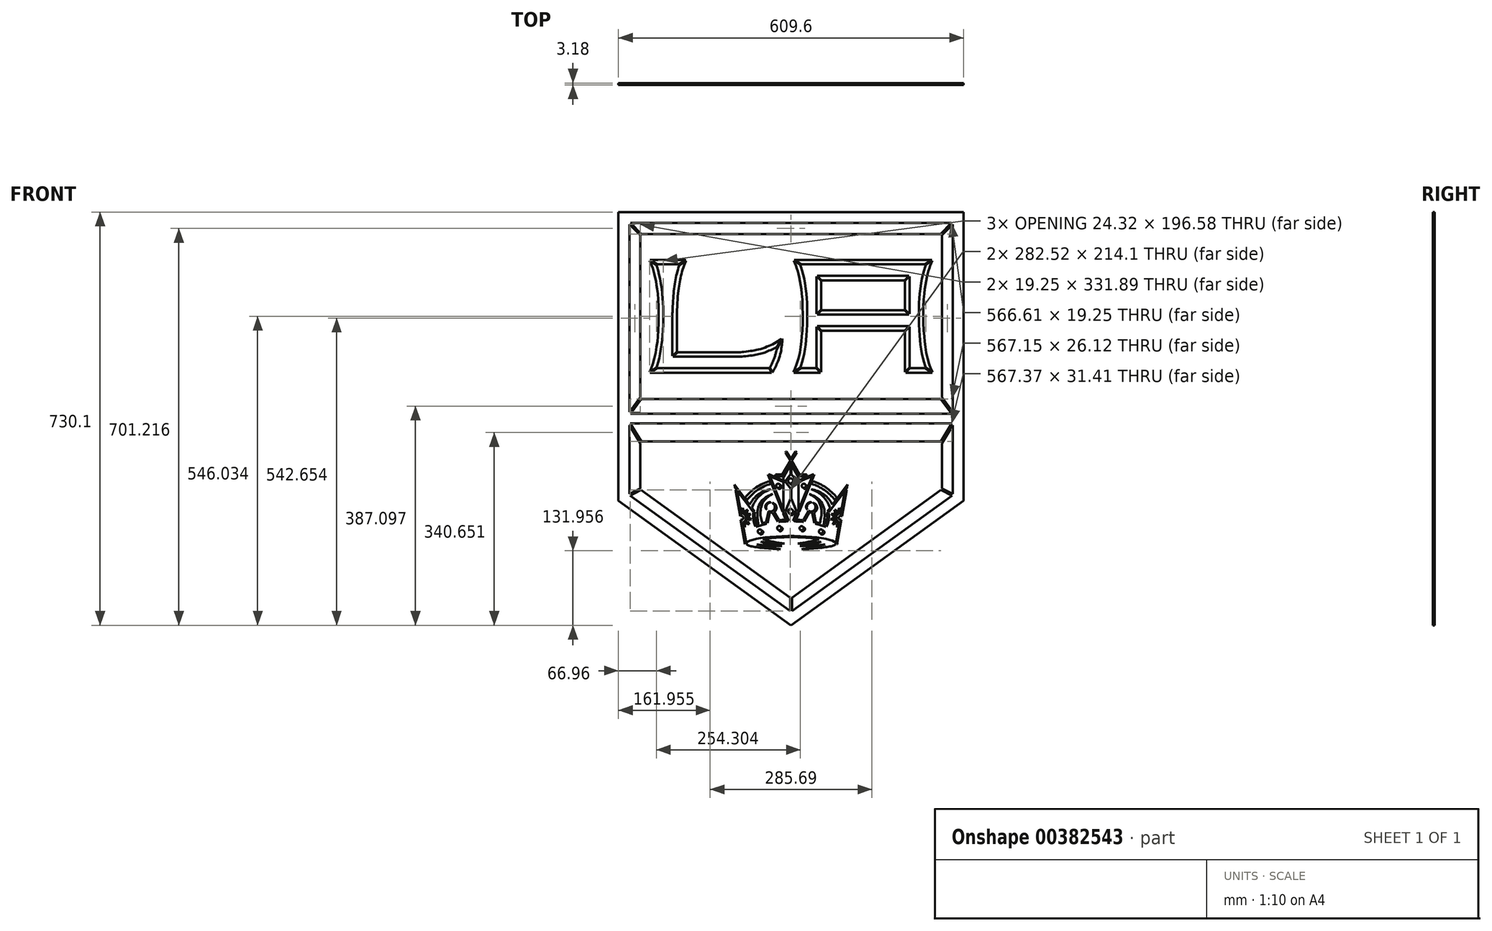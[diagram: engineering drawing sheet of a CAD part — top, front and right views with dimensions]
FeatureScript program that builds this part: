
annotation { "Feature Type Name" : "Feature", "Feature Type Description" : "" }
export const myFeature = defineFeature(function(context is Context, id is Id, definition is map)
    precondition{}
    {
        {
            var Q0;
            Q0=qCreatedBy(makeId("Front.planeOp"),FACE);
            var sketch = newSketch(context, id + "F0", { "sketchPlane" : qUnion([Q0])});
            skLineSegment(sketch, "E0", {"start": v(0, 0) * mm, "end": v(-304.8, 220.37) * mm});
            skLineSegment(sketch, "E1", {"start": v(-304.8, 220.37) * mm, "end": v(-304.8, 730.1) * mm});
            skLineSegment(sketch, "E2", {"start": v(-304.8, 730.1) * mm, "end": v(304.8, 730.1) * mm});
            skLineSegment(sketch, "E3", {"start": v(-1.59, 24.9) * mm, "end": v(-284.1, 229.17) * mm});
            skLineSegment(sketch, "E4", {"start": v(-1.59, 48.66) * mm, "end": v(-264.85, 239) * mm});
            skLineSegment(sketch, "E5", {"start": v(-285.55, 232) * mm, "end": v(-285.55, 353.32) * mm});
            skLineSegment(sketch, "E6", {"start": v(-266.3, 241.83) * mm, "end": v(-266.3, 321.91) * mm});
            skLineSegment(sketch, "E7", {"start": v(264.43, 324.95) * mm, "end": v(-264.43, 324.95) * mm});
            skLineSegment(sketch, "E8", {"start": v(283.69, 356.35) * mm, "end": v(-283.69, 356.35) * mm});
            skLineSegment(sketch, "E9", {"start": v(283.58, 374.04) * mm, "end": v(-283.58, 374.04) * mm});
            skLineSegment(sketch, "E10", {"start": v(264.32, 400.16) * mm, "end": v(-264.32, 400.16) * mm});
            skLineSegment(sketch, "E11", {"start": v(-283.3, 710.84) * mm, "end": v(283.3, 710.84) * mm});
            skLineSegment(sketch, "E12", {"start": v(-264.05, 691.59) * mm, "end": v(264.05, 691.59) * mm});
            skLineSegment(sketch, "E13", {"start": v(304.8, 220.37) * mm, "end": v(304.8, 730.1) * mm});
            skLineSegment(sketch, "E14", {"start": v(1.59, 24.9) * mm, "end": v(284.1, 229.17) * mm});
            skLineSegment(sketch, "E15", {"start": v(1.59, 48.66) * mm, "end": v(264.85, 239) * mm});
            skLineSegment(sketch, "E16", {"start": v(285.55, 232) * mm, "end": v(285.55, 353.32) * mm});
            skLineSegment(sketch, "E17", {"start": v(266.3, 241.83) * mm, "end": v(266.3, 321.91) * mm});
            skLineSegment(sketch, "E18", {"start": v(285.55, 376.71) * mm, "end": v(285.55, 708.6) * mm});
            skLineSegment(sketch, "E19", {"start": v(266.3, 402.83) * mm, "end": v(266.3, 689.34) * mm});
            skLineSegment(sketch, "E20", {"start": v(-285.55, 376.71) * mm, "end": v(-285.55, 708.6) * mm});
            skLineSegment(sketch, "E21", {"start": v(-266.3, 402.83) * mm, "end": v(-266.3, 689.34) * mm});
            skFitSpline(sketch, "E22", {"points": [v(-250, 447.75) * mm, v(-248.85, 449.98) * mm, v(-246.49, 454.7) * mm, v(-243.62, 462.95) * mm, v(-240.96, 472.2) * mm, v(-238.59, 483.4) * mm, v(-237.2, 493.08) * mm, v(-235.86, 501.9) * mm, v(-235.2, 509.36) * mm, v(-234.44, 519.64) * mm, v(-233.5, 537.38) * mm, v(-233.7, 556.74) * mm, v(-234.2, 574.6) * mm, v(-235.16, 584.45) * mm, v(-236.1, 591.32) * mm, v(-236.62, 596.69) * mm, v(-237.49, 601.42) * mm, v(-238.28, 606.78) * mm, v(-239.24, 611.8) * mm, v(-240.2, 616.28) * mm, v(-241.07, 619.38) * mm, v(-241.6, 622.23) * mm, v(-242.48, 624.82) * mm, v(-242.97, 627.3) * mm, v(-243.89, 629.6) * mm, v(-244.64, 631.93) * mm, v(-245.3, 634.07) * mm, v(-246, 635.97) * mm, v(-246.68, 637.82) * mm, v(-247.93, 640.58) * mm, v(-248.84, 642.79) * mm, v(-249.56, 644.32) * mm]});
            skFitSpline(sketch, "E23", {"points": [v(-185.13, 644.3) * mm, v(-185.73, 643.2) * mm, v(-186.9, 640.95) * mm, v(-188.33, 637.53) * mm, v(-189.8, 633.78) * mm, v(-190.93, 630.19) * mm, v(-192.11, 626.14) * mm, v(-193.33, 621.76) * mm, v(-194.58, 617.13) * mm, v(-195.4, 612.86) * mm, v(-196.19, 609.14) * mm, v(-196.86, 605.16) * mm, v(-197.56, 600.86) * mm, v(-198.28, 595.98) * mm, v(-198.96, 590.3) * mm, v(-199.73, 582.95) * mm, v(-200.48, 573.3) * mm, v(-201.11, 561.51) * mm, v(-201.45, 552.88) * mm, v(-201.47, 548.46) * mm]});
            skLineSegment(sketch, "E24", {"start": v(-201.47, 548.46) * mm, "end": v(-201.47, 483.77) * mm});
            skLineSegment(sketch, "E25", {"start": v(-200.4, 482.7) * mm, "end": v(-88.87, 482.7) * mm});
            skFitSpline(sketch, "E26", {"points": [v(-88.87, 482.7) * mm, v(-85.24, 482.97) * mm, v(-79.56, 483.4) * mm, v(-72.53, 484.53) * mm, v(-67.84, 485.1) * mm, v(-64.14, 485.99) * mm, v(-60.81, 486.73) * mm, v(-54.68, 487.7) * mm, v(-47.88, 489.83) * mm, v(-41.15, 492.84) * mm, v(-35.57, 494.86) * mm, v(-30.18, 497.95) * mm, v(-24.59, 500.93) * mm, v(-20.7, 504.2) * mm, v(-18.31, 505.7) * mm, v(-17.31, 506.57) * mm]});
            skFitSpline(sketch, "E27", {"points": [v(-15.59, 506.6) * mm, v(-15.55, 504.5) * mm, v(-15.55, 500.41) * mm, v(-16.7, 492.3) * mm, v(-18.23, 482) * mm, v(-21.17, 471.92) * mm, v(-24.25, 463.71) * mm, v(-27.07, 457.54) * mm, v(-29.96, 451.9) * mm, v(-32, 448.5) * mm, v(-32.88, 447.14) * mm]});
            skLineSegment(sketch, "E28", {"start": v(-34.23, 446.42) * mm, "end": v(-249.23, 446.42) * mm});
            skLineSegment(sketch, "E29", {"start": v(-248.81, 645.66) * mm, "end": v(-185.84, 645.66) * mm});
            skFitSpline(sketch, "E30", {"points": [v(4.3, 447.75) * mm, v(5.45, 449.98) * mm, v(7.82, 454.7) * mm, v(10.68, 462.95) * mm, v(13.35, 472.2) * mm, v(15.72, 483.4) * mm, v(17.1, 493.08) * mm, v(18.44, 501.9) * mm, v(19.1, 509.36) * mm, v(19.87, 519.64) * mm, v(20.8, 537.38) * mm, v(20.6, 556.74) * mm, v(20.1, 574.6) * mm, v(19.15, 584.45) * mm, v(18.21, 591.32) * mm, v(17.69, 596.69) * mm, v(16.82, 601.42) * mm, v(16.02, 606.78) * mm, v(15.06, 611.8) * mm, v(14.1, 616.28) * mm, v(13.23, 619.38) * mm, v(12.7, 622.23) * mm, v(11.83, 624.82) * mm, v(11.34, 627.3) * mm, v(10.42, 629.6) * mm, v(9.67, 631.93) * mm, v(9, 634.07) * mm, v(8.3, 635.97) * mm, v(7.63, 637.82) * mm, v(6.38, 640.58) * mm, v(5.47, 642.79) * mm, v(4.74, 644.32) * mm]});
            skLineSegment(sketch, "E31", {"start": v(5.5, 645.66) * mm, "end": v(248.81, 645.66) * mm});
            skLineSegment(sketch, "E32", {"start": v(249.23, 446.42) * mm, "end": v(202.36, 446.42) * mm});
            skFitSpline(sketch, "E33", {"points": [v(250, 447.75) * mm, v(248.85, 449.98) * mm, v(246.49, 454.7) * mm, v(243.62, 462.95) * mm, v(240.96, 472.2) * mm, v(238.59, 483.4) * mm, v(237.2, 493.08) * mm, v(235.86, 501.9) * mm, v(235.2, 509.36) * mm, v(234.44, 519.64) * mm, v(233.5, 537.38) * mm, v(233.7, 556.74) * mm, v(234.2, 574.6) * mm, v(235.16, 584.45) * mm, v(236.1, 591.32) * mm, v(236.62, 596.69) * mm, v(237.49, 601.42) * mm, v(238.28, 606.78) * mm, v(239.24, 611.8) * mm, v(240.2, 616.28) * mm, v(241.07, 619.38) * mm, v(241.6, 622.23) * mm, v(242.48, 624.82) * mm, v(242.97, 627.3) * mm, v(243.89, 629.6) * mm, v(244.64, 631.93) * mm, v(245.3, 634.07) * mm, v(246, 635.97) * mm, v(246.68, 637.82) * mm, v(247.93, 640.58) * mm, v(248.84, 642.79) * mm, v(249.56, 644.32) * mm]});
            skLineSegment(sketch, "E34", {"start": v(54.1, 609.59) * mm, "end": v(200.2, 609.59) * mm});
            skLineSegment(sketch, "E35", {"start": v(54.1, 556.91) * mm, "end": v(200.2, 556.91) * mm});
            skLineSegment(sketch, "E36", {"start": v(54.1, 520.58) * mm, "end": v(200.2, 520.58) * mm});
            skLineSegment(sketch, "E37", {"start": v(53.02, 447.5) * mm, "end": v(53.02, 519.5) * mm});
            skLineSegment(sketch, "E38", {"start": v(201.28, 447.5) * mm, "end": v(201.28, 519.5) * mm});
            skLineSegment(sketch, "E39", {"start": v(51.94, 446.42) * mm, "end": v(5.07, 446.42) * mm});
            skLineSegment(sketch, "E40", {"start": v(53.02, 558) * mm, "end": v(53.02, 608.5) * mm});
            skLineSegment(sketch, "E41", {"start": v(201.28, 558) * mm, "end": v(201.28, 608.5) * mm});
            skLineSegment(sketch, "E42", {"start": v(-8.97, 307.2) * mm, "end": v(-9.82, 305.39) * mm});
            skLineSegment(sketch, "E43", {"start": v(-8.25, 307.2) * mm, "end": v(-8.97, 307.2) * mm});
            skLineSegment(sketch, "E44", {"start": v(-1.08, 291.22) * mm, "end": v(-15.16, 266.73) * mm});
            skLineSegment(sketch, "E45", {"start": v(-99.7, 248.48) * mm, "end": v(-98.64, 242.38) * mm});
            skArc(sketch, "E46", {"start": v(-36.02, 249.87) * mm, "mid": v(-59.07, 238.98) * mm, "end": v(-77.5, 221.37) * mm});
            skLineSegment(sketch, "E47", {"start": v(-14.4, 263.48) * mm, "end": v(-26.33, 263.48) * mm});
            skLineSegment(sketch, "E48", {"start": v(-27.56, 266.73) * mm, "end": v(-15.16, 266.73) * mm});
            skLineSegment(sketch, "E49", {"start": v(-1.08, 291.22) * mm, "end": v(-9.82, 305.39) * mm});
            skArc(sketch, "E50", {"start": v(-27.56, 266.73) * mm, "mid": v(-27.25, 265) * mm, "end": v(-26.33, 263.48) * mm});
            skCircle(sketch, "E51", {"center": v(-20.88, 171.82) * mm, "radius": 3.66 * mm});
            skArc(sketch, "E52", {"start": v(-20.53, 166.47) * mm, "mid": v(-15.9, 167.81) * mm, "end": v(-15.58, 172.62) * mm});
            skArc(sketch, "E53", {"start": v(-20.45, 166.95) * mm, "mid": v(-16.9, 168.62) * mm, "end": v(-16.03, 172.44) * mm});
            skCircle(sketch, "E54", {"center": v(-55.14, 165.94) * mm, "radius": 3.66 * mm});
            skArc(sketch, "E55", {"start": v(-54.79, 160.6) * mm, "mid": v(-50.17, 161.93) * mm, "end": v(-49.84, 166.74) * mm});
            skArc(sketch, "E56", {"start": v(-54.7, 161.07) * mm, "mid": v(-51.16, 162.74) * mm, "end": v(-50.29, 166.56) * mm});
            skCircle(sketch, "E57", {"center": v(18.65, 171.41) * mm, "radius": 3.66 * mm});
            skArc(sketch, "E58", {"start": v(19, 166.06) * mm, "mid": v(23.62, 167.4) * mm, "end": v(23.95, 172.21) * mm});
            skArc(sketch, "E59", {"start": v(19.08, 166.54) * mm, "mid": v(22.62, 168.21) * mm, "end": v(23.5, 172.03) * mm});
            skCircle(sketch, "E60", {"center": v(52.9, 165.74) * mm, "radius": 3.66 * mm});
            skArc(sketch, "E61", {"start": v(53.25, 160.39) * mm, "mid": v(57.88, 161.73) * mm, "end": v(58.2, 166.54) * mm});
            skArc(sketch, "E62", {"start": v(53.34, 160.87) * mm, "mid": v(56.88, 162.54) * mm, "end": v(57.76, 166.35) * mm});
            skLineSegment(sketch, "E63", {"start": v(-10.12, 200.44) * mm, "end": v(-3.9, 184.71) * mm});
            skLineSegment(sketch, "E64", {"start": v(-13.2, 262.24) * mm, "end": v(-13.2, 254.89) * mm});
            skLineSegment(sketch, "E65", {"start": v(-10.12, 200.44) * mm, "end": v(-0.8, 224.23) * mm});
            skLineSegment(sketch, "E66", {"start": v(-0.83, 242.03) * mm, "end": v(-9.69, 253.36) * mm});
            skLineSegment(sketch, "E67", {"start": v(-9.72, 254.89) * mm, "end": v(-0.77, 267.03) * mm});
            skLineSegment(sketch, "E68", {"start": v(-67.1, 200.23) * mm, "end": v(-98.64, 242.38) * mm});
            skLineSegment(sketch, "E69", {"start": v(-41.4, 180.52) * mm, "end": v(-37.35, 199.4) * mm});
            skLineSegment(sketch, "E70", {"start": v(-23.32, 183.5) * mm, "end": v(-32.34, 199.14) * mm});
            skArc(sketch, "E71", {"start": v(-35.66, 240.3) * mm, "mid": v(-57.84, 231.32) * mm, "end": v(-73.04, 212.85) * mm});
            skArc(sketch, "E72", {"start": v(-35.66, 240.3) * mm, "mid": v(-56.4, 227.88) * mm, "end": v(-68.76, 207.13) * mm});
            skFitSpline(sketch, "E73", {"points": [v(-57.64, 178.2) * mm, v(-58.15, 181.73) * mm, v(-58.83, 186.44) * mm, v(-59.3, 192.88) * mm, v(-59.13, 198) * mm, v(-58.83, 204.6) * mm, v(-56.44, 211.6) * mm, v(-53.24, 218.03) * mm, v(-49.21, 222.9) * mm, v(-45.11, 225.83) * mm, v(-41.43, 228.15) * mm, v(-37.96, 229.83) * mm, v(-34.88, 231.18) * mm, v(-33.12, 232.05) * mm, v(-32.45, 232.27) * mm]});
            skFitSpline(sketch, "E74", {"points": [v(-50.57, 180.3) * mm, v(-51.06, 181.94) * mm, v(-51.9, 184.73) * mm, v(-52.95, 189.65) * mm, v(-53.9, 194.7) * mm, v(-54.07, 201.3) * mm, v(-53, 208.15) * mm, v(-50.8, 215) * mm, v(-47.57, 220.43) * mm, v(-43.97, 223.96) * mm, v(-40.7, 226.81) * mm, v(-37.52, 229.01) * mm, v(-34.68, 230.81) * mm, v(-33.08, 231.95) * mm, v(-32.45, 232.27) * mm]});
            skFitSpline(sketch, "E75", {"points": [v(-61.5, 178.07) * mm, v(-61.54, 178.18) * mm, v(-61.66, 178.53) * mm, v(-61.93, 179.38) * mm, v(-62.27, 180.65) * mm, v(-62.63, 182.23) * mm, v(-62.96, 183.85) * mm, v(-63.25, 185.47) * mm, v(-63.5, 187.1) * mm, v(-63.7, 188.73) * mm, v(-63.87, 190.36) * mm, v(-63.98, 191.98) * mm, v(-64.05, 193.61) * mm, v(-64.06, 195.23) * mm, v(-64, 196.85) * mm, v(-63.92, 198.26) * mm, v(-63.84, 199.14) * mm, v(-63.8, 199.55) * mm]});
            skLineSegment(sketch, "E76", {"start": v(-43.77, 182.87) * mm, "end": v(-39.73, 201.67) * mm});
            skArc(sketch, "E77", {"start": v(-42.48, 179.44) * mm, "mid": v(-52.12, 176.95) * mm, "end": v(-61.6, 173.9) * mm});
            skArc(sketch, "E78", {"start": v(-5.27, 183.67) * mm, "mid": v(-13.62, 183.44) * mm, "end": v(-21.95, 182.8) * mm});
            skLineSegment(sketch, "E79", {"start": v(-21.8, 186.47) * mm, "end": v(-29.73, 200.25) * mm});
            skArc(sketch, "E80", {"start": v(-10.92, 186.37) * mm, "mid": v(-15.68, 186.13) * mm, "end": v(-20.43, 185.77) * mm});
            skArc(sketch, "E81", {"start": v(-36.23, 217.43) * mm, "mid": v(-44.04, 213.72) * mm, "end": v(-43.84, 205.07) * mm});
            skArc(sketch, "E82", {"start": v(-39.73, 201.67) * mm, "mid": v(-29.53, 205.2) * mm, "end": v(-32.24, 215.64) * mm});
            skArc(sketch, "E83", {"start": v(-36.23, 216.95) * mm, "mid": v(-42.62, 212.84) * mm, "end": v(-43.4, 205.3) * mm});
            skArc(sketch, "E84", {"start": v(-29.73, 200.25) * mm, "mid": v(-25.75, 208.92) * mm, "end": v(-32.04, 216.09) * mm});
            skArc(sketch, "E85", {"start": v(-37.35, 199.4) * mm, "mid": v(-34.86, 198.9) * mm, "end": v(-32.34, 199.14) * mm});
            skArc(sketch, "E86", {"start": v(30.92, 202.32) * mm, "mid": v(41.97, 204.61) * mm, "end": v(39.6, 215.64) * mm});
            skArc(sketch, "E87", {"start": v(40.23, 199.36) * mm, "mid": v(46.18, 207.88) * mm, "end": v(39.8, 216.09) * mm});
            skArc(sketch, "E88", {"start": v(32.9, 200.14) * mm, "mid": v(35.1, 199.2) * mm, "end": v(37.46, 198.9) * mm});
            skArc(sketch, "E89", {"start": v(35.61, 217.43) * mm, "mid": v(27.8, 213.72) * mm, "end": v(28, 205.07) * mm});
            skArc(sketch, "E90", {"start": v(35.6, 216.95) * mm, "mid": v(29.22, 212.84) * mm, "end": v(28.44, 205.3) * mm});
            skArc(sketch, "E91", {"start": v(-84.78, 202.13) * mm, "mid": v(-86.49, 202.43) * mm, "end": v(-88.22, 202.5) * mm});
            skArc(sketch, "E92", {"start": v(-88.9, 186.31) * mm, "mid": v(-84.25, 190.41) * mm, "end": v(-90, 192.71) * mm});
            skArc(sketch, "E93", {"start": v(-83.6, 179.69) * mm, "mid": v(-77.04, 191.67) * mm, "end": v(-87.25, 200.73) * mm});
            skArc(sketch, "E94", {"start": v(-83.86, 181.2) * mm, "mid": v(-78.5, 191.41) * mm, "end": v(-86.99, 199.22) * mm});
            skArc(sketch, "E95", {"start": v(-85.53, 181.9) * mm, "mid": v(-79.74, 191.2) * mm, "end": v(-88.33, 197.99) * mm});
            skLineSegment(sketch, "E96", {"start": v(-94.68, 234.53) * mm, "end": v(-88.33, 197.99) * mm});
            skLineSegment(sketch, "E97", {"start": v(-85.53, 181.9) * mm, "end": v(-84.76, 177.46) * mm});
            skFitSpline(sketch, "E98", {"points": [v(-63.02, 174.48) * mm, v(-63.38, 175.26) * mm, v(-64.42, 177.58) * mm, v(-65.69, 182.73) * mm, v(-66.72, 189.18) * mm, v(-66.93, 194.9) * mm, v(-66.76, 197.89) * mm, v(-66.69, 198.76) * mm]});
            skArc(sketch, "E99", {"start": v(-57.64, 178.2) * mm, "mid": v(-58.88, 177.8) * mm, "end": v(-60.12, 177.38) * mm});
            skArc(sketch, "E100", {"start": v(-44.84, 181.77) * mm, "mid": v(-47.7, 181.06) * mm, "end": v(-50.57, 180.3) * mm});
            skLineSegment(sketch, "E101", {"start": v(-64.2, 201.02) * mm, "end": v(-68.76, 207.13) * mm});
            skArc(sketch, "E102", {"start": v(-37.91, 254.65) * mm, "mid": v(-61.56, 243.47) * mm, "end": v(-80.68, 225.62) * mm});
            skLineSegment(sketch, "E103", {"start": v(-73.04, 212.85) * mm, "end": v(-99.7, 248.48) * mm});
            skLineSegment(sketch, "E104", {"start": v(236.57, 637.72) * mm, "end": v(248.81, 645.66) * mm});
            skLineSegment(sketch, "E105", {"start": v(237.9, 636.76) * mm, "end": v(249.56, 644.32) * mm});
            skLineSegment(sketch, "E106", {"start": v(17.74, 637.72) * mm, "end": v(5.5, 645.66) * mm});
            skLineSegment(sketch, "E107", {"start": v(16.41, 636.76) * mm, "end": v(4.74, 644.32) * mm});
            skLineSegment(sketch, "E108", {"start": v(4.3, 447.75) * mm, "end": v(16.36, 455.24) * mm});
            skLineSegment(sketch, "E109", {"start": v(5.07, 446.42) * mm, "end": v(17.84, 454.36) * mm});
            skLineSegment(sketch, "E110", {"start": v(45.08, 550.06) * mm, "end": v(53.02, 558) * mm});
            skLineSegment(sketch, "E111", {"start": v(46.17, 548.98) * mm, "end": v(54.1, 556.91) * mm});
            skLineSegment(sketch, "E112", {"start": v(45.08, 616.44) * mm, "end": v(53.02, 608.5) * mm});
            skLineSegment(sketch, "E113", {"start": v(46.17, 617.52) * mm, "end": v(54.1, 609.59) * mm});
            skLineSegment(sketch, "E114", {"start": v(200.2, 609.59) * mm, "end": v(208.14, 617.52) * mm});
            skLineSegment(sketch, "E115", {"start": v(201.28, 608.5) * mm, "end": v(209.22, 616.44) * mm});
            skLineSegment(sketch, "E116", {"start": v(209.22, 550.06) * mm, "end": v(201.28, 558) * mm});
            skLineSegment(sketch, "E117", {"start": v(208.14, 548.98) * mm, "end": v(200.2, 556.91) * mm});
            skLineSegment(sketch, "E118", {"start": v(44, 454.36) * mm, "end": v(51.94, 446.42) * mm});
            skLineSegment(sketch, "E119", {"start": v(45.08, 455.44) * mm, "end": v(53.02, 447.5) * mm});
            skLineSegment(sketch, "E120", {"start": v(45.08, 527.44) * mm, "end": v(53.02, 519.5) * mm});
            skLineSegment(sketch, "E121", {"start": v(46.17, 528.52) * mm, "end": v(54.1, 520.58) * mm});
            skLineSegment(sketch, "E122", {"start": v(200.2, 520.58) * mm, "end": v(208.14, 528.52) * mm});
            skLineSegment(sketch, "E123", {"start": v(201.28, 519.5) * mm, "end": v(209.22, 527.44) * mm});
            skLineSegment(sketch, "E124", {"start": v(209.22, 455.44) * mm, "end": v(201.28, 447.5) * mm});
            skLineSegment(sketch, "E125", {"start": v(210.3, 454.36) * mm, "end": v(202.36, 446.42) * mm});
            skLineSegment(sketch, "E126", {"start": v(250, 447.75) * mm, "end": v(237.94, 455.24) * mm});
            skLineSegment(sketch, "E127", {"start": v(249.23, 446.42) * mm, "end": v(236.47, 454.36) * mm});
            skLineSegment(sketch, "E128", {"start": v(-32.88, 447.14) * mm, "end": v(-37.28, 455.2) * mm});
            skLineSegment(sketch, "E129", {"start": v(-34.23, 446.42) * mm, "end": v(-38.57, 454.36) * mm});
            skLineSegment(sketch, "E130", {"start": v(-24.68, 491.88) * mm, "end": v(-17.31, 506.57) * mm});
            skLineSegment(sketch, "E131", {"start": v(-25.73, 486.38) * mm, "end": v(-15.59, 506.6) * mm});
            skLineSegment(sketch, "E132", {"start": v(-209.41, 475.84) * mm, "end": v(-201.47, 483.77) * mm});
            skLineSegment(sketch, "E133", {"start": v(-208.3, 474.78) * mm, "end": v(-200.4, 482.7) * mm});
            skLineSegment(sketch, "E134", {"start": v(-198.67, 637.72) * mm, "end": v(-185.84, 645.66) * mm});
            skLineSegment(sketch, "E135", {"start": v(-197.05, 636.93) * mm, "end": v(-185.13, 644.3) * mm});
            skLineSegment(sketch, "E136", {"start": v(-236.57, 637.72) * mm, "end": v(-248.81, 645.66) * mm});
            skLineSegment(sketch, "E137", {"start": v(-237.9, 636.76) * mm, "end": v(-249.56, 644.32) * mm});
            skLineSegment(sketch, "E138", {"start": v(-236.47, 454.36) * mm, "end": v(-249.23, 446.42) * mm});
            skLineSegment(sketch, "E139", {"start": v(-237.94, 455.24) * mm, "end": v(-250, 447.75) * mm});
            skLineSegment(sketch, "E140", {"start": v(0, 293.83) * mm, "end": v(-8.25, 307.2) * mm});
            skLineSegment(sketch, "E141", {"start": v(10.12, 200.44) * mm, "end": v(0.8, 224.23) * mm});
            skLineSegment(sketch, "E142", {"start": v(0, 288.5) * mm, "end": v(-14.4, 263.48) * mm});
            skLineSegment(sketch, "E143", {"start": v(-0.77, 283.92) * mm, "end": v(-13.17, 262.36) * mm});
            skLineSegment(sketch, "E144", {"start": v(-88.9, 186.31) * mm, "end": v(-81.43, 143.36) * mm});
            skLineSegment(sketch, "E145", {"start": v(-73.66, 178.5) * mm, "end": v(-79.46, 180.22) * mm});
            skLineSegment(sketch, "E146", {"start": v(-73.66, 178.5) * mm, "end": v(-76.63, 183.78) * mm});
            skArc(sketch, "E147", {"start": v(-79.46, 180.22) * mm, "mid": v(-77.89, 181.87) * mm, "end": v(-76.63, 183.78) * mm});
            skLineSegment(sketch, "E148", {"start": v(-84.6, 176.5) * mm, "end": v(-79.66, 148.12) * mm});
            skLineSegment(sketch, "E149", {"start": v(-69.91, 187.1) * mm, "end": v(-75.8, 185.69) * mm});
            skLineSegment(sketch, "E150", {"start": v(-69.91, 187.1) * mm, "end": v(-75.13, 190.18) * mm});
            skArc(sketch, "E151", {"start": v(-75.8, 185.69) * mm, "mid": v(-75.26, 187.9) * mm, "end": v(-75.13, 190.18) * mm});
            skLineSegment(sketch, "E152", {"start": v(-70.97, 196.42) * mm, "end": v(-75.36, 192.25) * mm});
            skLineSegment(sketch, "E153", {"start": v(-70.97, 196.42) * mm, "end": v(-77.02, 196.48) * mm});
            skArc(sketch, "E154", {"start": v(-75.36, 192.25) * mm, "mid": v(-76, 194.44) * mm, "end": v(-77.02, 196.48) * mm});
            skLineSegment(sketch, "E155", {"start": v(-76.54, 203.97) * mm, "end": v(-78.26, 198.16) * mm});
            skLineSegment(sketch, "E156", {"start": v(-76.54, 203.97) * mm, "end": v(-81.82, 201) * mm});
            skArc(sketch, "E157", {"start": v(-78.26, 198.16) * mm, "mid": v(-79.91, 199.74) * mm, "end": v(-81.82, 201) * mm});
            skLineSegment(sketch, "E158", {"start": v(-85.14, 207.71) * mm, "end": v(-83.73, 201.82) * mm});
            skLineSegment(sketch, "E159", {"start": v(-85.14, 207.71) * mm, "end": v(-88.22, 202.5) * mm});
            skArc(sketch, "E160", {"start": v(-83.73, 201.82) * mm, "mid": v(-85.95, 202.36) * mm, "end": v(-88.22, 202.5) * mm});
            skLineSegment(sketch, "E161", {"start": v(-81.2, 172.93) * mm, "end": v(-84.6, 176.5) * mm});
            skLineSegment(sketch, "E162", {"start": v(-81.2, 172.93) * mm, "end": v(-81.14, 178.98) * mm});
            skArc(sketch, "E163", {"start": v(-84.76, 177.46) * mm, "mid": v(-82.9, 178.08) * mm, "end": v(-81.14, 178.98) * mm});
            skLineSegment(sketch, "E164", {"start": v(-83.86, 181.2) * mm, "end": v(-83.6, 179.69) * mm});
            skLineSegment(sketch, "E165", {"start": v(-87.25, 200.73) * mm, "end": v(-86.99, 199.22) * mm});
            skLineSegment(sketch, "E166", {"start": v(-94.68, 234.53) * mm, "end": v(-98.06, 239.05) * mm});
            skLineSegment(sketch, "E167", {"start": v(-98.06, 239.05) * mm, "end": v(-90, 192.71) * mm});
            skLineSegment(sketch, "E168", {"start": v(-67.1, 200.23) * mm, "end": v(-64.2, 201.02) * mm});
            skLineSegment(sketch, "E169", {"start": v(-66.69, 198.76) * mm, "end": v(-63.8, 199.55) * mm});
            skLineSegment(sketch, "E170", {"start": v(-61.5, 178.07) * mm, "end": v(-63.02, 174.48) * mm});
            skLineSegment(sketch, "E171", {"start": v(-60.12, 177.38) * mm, "end": v(-61.6, 173.9) * mm});
            skLineSegment(sketch, "E172", {"start": v(-44.84, 181.77) * mm, "end": v(-42.48, 179.44) * mm});
            skLineSegment(sketch, "E173", {"start": v(-43.77, 182.87) * mm, "end": v(-41.4, 180.52) * mm});
            skArc(sketch, "E174", {"start": v(-43.84, 205.07) * mm, "mid": v(-43.52, 205) * mm, "end": v(-43.4, 205.3) * mm});
            skArc(sketch, "E175", {"start": v(-36.23, 217.43) * mm, "mid": v(-36.02, 217.2) * mm, "end": v(-36.23, 216.95) * mm});
            skArc(sketch, "E176", {"start": v(-32.24, 215.64) * mm, "mid": v(-32.33, 215.95) * mm, "end": v(-32.04, 216.09) * mm});
            skLineSegment(sketch, "E177", {"start": v(-77.5, 221.37) * mm, "end": v(-80.68, 225.62) * mm});
            skLineSegment(sketch, "E178", {"start": v(-37.91, 254.65) * mm, "end": v(-36.02, 249.87) * mm});
            skLineSegment(sketch, "E179", {"start": v(-21.8, 186.47) * mm, "end": v(-23.32, 183.5) * mm});
            skLineSegment(sketch, "E180", {"start": v(-20.43, 185.77) * mm, "end": v(-21.95, 182.8) * mm});
            skLineSegment(sketch, "E181", {"start": v(-3.9, 184.71) * mm, "end": v(-9.67, 187.47) * mm});
            skLineSegment(sketch, "E182", {"start": v(-5.27, 183.67) * mm, "end": v(-10.92, 186.37) * mm});
            skArc(sketch, "E183", {"start": v(-20.3, 185.78) * mm, "mid": v(-20.41, 185.74) * mm, "end": v(-20.5, 185.65) * mm});
            skCircle(sketch, "E184", {"center": v(-22.64, 246.5) * mm, "radius": 3.66 * mm});
            skArc(sketch, "E185", {"start": v(-22.3, 241.15) * mm, "mid": v(-17.67, 242.5) * mm, "end": v(-17.34, 247.3) * mm});
            skArc(sketch, "E186", {"start": v(-22.2, 241.62) * mm, "mid": v(-18.67, 243.3) * mm, "end": v(-17.79, 247.11) * mm});
            skLineSegment(sketch, "E187", {"start": v(-14.73, 256.34) * mm, "end": v(-14.73, 253.63) * mm});
            skLineSegment(sketch, "E188", {"start": v(-0.77, 283.92) * mm, "end": v(-0.77, 267.03) * mm});
            skLineSegment(sketch, "E189", {"start": v(-14.73, 206.61) * mm, "end": v(-14.73, 200.27) * mm});
            skLineSegment(sketch, "E190", {"start": v(-13.2, 196.4) * mm, "end": v(-9.67, 187.47) * mm});
            skCircle(sketch, "E191", {"center": v(-0.7, 201.3) * mm, "radius": 4.36 * mm});
            skArc(sketch, "E192", {"start": v(-1.14, 196.08) * mm, "mid": v(3.26, 196.97) * mm, "end": v(4.54, 201.27) * mm});
            skArc(sketch, "E193", {"start": v(-1.37, 195.66) * mm, "mid": v(4.27, 195.87) * mm, "end": v(4.99, 201.46) * mm});
            skArc(sketch, "E194", {"start": v(-1.14, 196.08) * mm, "mid": v(-1.43, 195.97) * mm, "end": v(-1.37, 195.66) * mm});
            skArc(sketch, "E195", {"start": v(4.99, 201.46) * mm, "mid": v(4.68, 201.55) * mm, "end": v(4.54, 201.27) * mm});
            skArc(sketch, "E196", {"start": v(-54.7, 161.07) * mm, "mid": v(-54.95, 160.86) * mm, "end": v(-54.79, 160.6) * mm});
            skArc(sketch, "E197", {"start": v(-49.84, 166.74) * mm, "mid": v(-50.14, 166.84) * mm, "end": v(-50.29, 166.56) * mm});
            skArc(sketch, "E198", {"start": v(-20.45, 166.95) * mm, "mid": v(-20.7, 166.74) * mm, "end": v(-20.53, 166.47) * mm});
            skArc(sketch, "E199", {"start": v(-15.58, 172.62) * mm, "mid": v(-15.88, 172.72) * mm, "end": v(-16.03, 172.44) * mm});
            skArc(sketch, "E200", {"start": v(19, 166.06) * mm, "mid": v(18.83, 166.34) * mm, "end": v(19.08, 166.54) * mm});
            skArc(sketch, "E201", {"start": v(23.95, 172.21) * mm, "mid": v(23.65, 172.31) * mm, "end": v(23.5, 172.03) * mm});
            skArc(sketch, "E202", {"start": v(53.34, 160.86) * mm, "mid": v(53.1, 160.66) * mm, "end": v(53.25, 160.39) * mm});
            skArc(sketch, "E203", {"start": v(58.2, 166.54) * mm, "mid": v(57.9, 166.64) * mm, "end": v(57.76, 166.35) * mm});
            skArc(sketch, "E204", {"start": v(39.6, 215.64) * mm, "mid": v(39.51, 215.95) * mm, "end": v(39.8, 216.09) * mm});
            skArc(sketch, "E205", {"start": v(28.44, 205.3) * mm, "mid": v(28.32, 205) * mm, "end": v(28, 205.07) * mm});
            skArc(sketch, "E206", {"start": v(35.61, 217.43) * mm, "mid": v(35.82, 217.2) * mm, "end": v(35.6, 216.95) * mm});
            skLineSegment(sketch, "E207", {"start": v(-9.72, 254.89) * mm, "end": v(-13.2, 254.89) * mm});
            skLineSegment(sketch, "E208", {"start": v(-9.69, 253.36) * mm, "end": v(-13.2, 253.36) * mm});
            skLineSegment(sketch, "E209", {"start": v(-13.2, 253.36) * mm, "end": v(-13.2, 196.4) * mm});
            skArc(sketch, "E210", {"start": v(-13.17, 262.36) * mm, "mid": v(-13.2, 262.3) * mm, "end": v(-13.2, 262.24) * mm});
            skLineSegment(sketch, "E211", {"start": v(8.97, 307.2) * mm, "end": v(9.82, 305.39) * mm});
            skLineSegment(sketch, "E212", {"start": v(8.25, 307.2) * mm, "end": v(8.97, 307.2) * mm});
            skLineSegment(sketch, "E213", {"start": v(1.08, 291.22) * mm, "end": v(15.16, 266.73) * mm});
            skLineSegment(sketch, "E214", {"start": v(14.4, 263.48) * mm, "end": v(26.33, 263.48) * mm});
            skLineSegment(sketch, "E215", {"start": v(27.56, 266.73) * mm, "end": v(15.16, 266.73) * mm});
            skLineSegment(sketch, "E216", {"start": v(1.08, 291.22) * mm, "end": v(9.82, 305.39) * mm});
            skArc(sketch, "E217", {"start": v(26.33, 263.48) * mm, "mid": v(27.25, 265) * mm, "end": v(27.56, 266.73) * mm});
            skLineSegment(sketch, "E218", {"start": v(67.1, 200.23) * mm, "end": v(98.64, 242.38) * mm});
            skArc(sketch, "E219", {"start": v(73.04, 212.85) * mm, "mid": v(57.84, 231.32) * mm, "end": v(35.66, 240.3) * mm});
            skArc(sketch, "E220", {"start": v(68.76, 207.13) * mm, "mid": v(56.4, 227.88) * mm, "end": v(35.66, 240.3) * mm});
            skFitSpline(sketch, "E221", {"points": [v(57.64, 178.2) * mm, v(58.15, 181.73) * mm, v(58.83, 186.44) * mm, v(59.3, 192.88) * mm, v(59.13, 198) * mm, v(58.83, 204.6) * mm, v(56.44, 211.6) * mm, v(53.24, 218.03) * mm, v(49.21, 222.9) * mm, v(45.11, 225.83) * mm, v(41.43, 228.15) * mm, v(37.96, 229.83) * mm, v(34.88, 231.18) * mm, v(33.12, 232.05) * mm, v(32.45, 232.27) * mm]});
            skFitSpline(sketch, "E222", {"points": [v(50.57, 180.3) * mm, v(51.06, 181.94) * mm, v(51.9, 184.73) * mm, v(52.95, 189.65) * mm, v(53.9, 194.7) * mm, v(54.07, 201.3) * mm, v(53, 208.15) * mm, v(50.8, 215) * mm, v(47.57, 220.43) * mm, v(43.97, 223.96) * mm, v(40.7, 226.81) * mm, v(37.52, 229.01) * mm, v(34.68, 230.81) * mm, v(33.08, 231.95) * mm, v(32.45, 232.27) * mm]});
            skLineSegment(sketch, "E223", {"start": v(73.04, 212.85) * mm, "end": v(99.7, 248.48) * mm});
            skLineSegment(sketch, "E224", {"start": v(0, 293.83) * mm, "end": v(8.25, 307.2) * mm});
            skLineSegment(sketch, "E225", {"start": v(0, 288.5) * mm, "end": v(14.4, 263.48) * mm});
            skLineSegment(sketch, "E226", {"start": v(0.77, 283.92) * mm, "end": v(13.17, 262.36) * mm});
            skLineSegment(sketch, "E227", {"start": v(94.68, 234.53) * mm, "end": v(88.33, 197.99) * mm});
            skLineSegment(sketch, "E228", {"start": v(94.68, 234.53) * mm, "end": v(98.06, 239.05) * mm});
            skLineSegment(sketch, "E229", {"start": v(98.06, 239.05) * mm, "end": v(90, 192.71) * mm});
            skLineSegment(sketch, "E230", {"start": v(99.7, 248.48) * mm, "end": v(98.64, 242.38) * mm});
            skLineSegment(sketch, "E231", {"start": v(37.91, 254.65) * mm, "end": v(36.02, 249.87) * mm});
            skArc(sketch, "E232", {"start": v(77.5, 221.37) * mm, "mid": v(59.07, 238.98) * mm, "end": v(36.02, 249.87) * mm});
            skArc(sketch, "E233", {"start": v(80.68, 225.62) * mm, "mid": v(61.56, 243.47) * mm, "end": v(37.91, 254.65) * mm});
            skLineSegment(sketch, "E234", {"start": v(14.73, 256.34) * mm, "end": v(14.73, 253.63) * mm});
            skLineSegment(sketch, "E235", {"start": v(14.73, 253.63) * mm, "end": v(35.44, 262.8) * mm});
            skLineSegment(sketch, "E236", {"start": v(14.73, 256.34) * mm, "end": v(39.8, 267.43) * mm});
            skLineSegment(sketch, "E237", {"start": v(0.77, 283.92) * mm, "end": v(0.77, 267.03) * mm});
            skLineSegment(sketch, "E238", {"start": v(36.5, 261.6) * mm, "end": v(14.73, 206.61) * mm});
            skLineSegment(sketch, "E239", {"start": v(40.86, 266.24) * mm, "end": v(14.73, 200.27) * mm});
            skLineSegment(sketch, "E240", {"start": v(9.72, 254.89) * mm, "end": v(13.2, 254.89) * mm});
            skLineSegment(sketch, "E241", {"start": v(9.69, 253.36) * mm, "end": v(13.2, 253.36) * mm});
            skLineSegment(sketch, "E242", {"start": v(0.83, 242.03) * mm, "end": v(9.69, 253.36) * mm});
            skLineSegment(sketch, "E243", {"start": v(9.72, 254.89) * mm, "end": v(0.77, 267.03) * mm});
            skLineSegment(sketch, "E244", {"start": v(13.2, 253.36) * mm, "end": v(13.2, 196.4) * mm});
            skLineSegment(sketch, "E245", {"start": v(13.2, 262.24) * mm, "end": v(13.2, 254.89) * mm});
            skArc(sketch, "E246", {"start": v(13.2, 262.24) * mm, "mid": v(13.2, 262.3) * mm, "end": v(13.17, 262.36) * mm});
            skLineSegment(sketch, "E247", {"start": v(10.12, 200.44) * mm, "end": v(3.9, 184.71) * mm});
            skLineSegment(sketch, "E248", {"start": v(23.32, 183.5) * mm, "end": v(32.9, 200.14) * mm});
            skArc(sketch, "E249", {"start": v(21.95, 182.8) * mm, "mid": v(13.62, 183.44) * mm, "end": v(5.27, 183.67) * mm});
            skLineSegment(sketch, "E250", {"start": v(21.8, 186.47) * mm, "end": v(30.92, 202.32) * mm});
            skArc(sketch, "E251", {"start": v(20.43, 185.77) * mm, "mid": v(15.68, 186.13) * mm, "end": v(10.92, 186.37) * mm});
            skArc(sketch, "E252", {"start": v(90, 192.71) * mm, "mid": v(84.25, 190.41) * mm, "end": v(88.9, 186.31) * mm});
            skArc(sketch, "E253", {"start": v(87.25, 200.73) * mm, "mid": v(77.04, 191.67) * mm, "end": v(83.6, 179.69) * mm});
            skLineSegment(sketch, "E254", {"start": v(73.66, 178.5) * mm, "end": v(79.46, 180.22) * mm});
            skLineSegment(sketch, "E255", {"start": v(73.66, 178.5) * mm, "end": v(76.63, 183.78) * mm});
            skArc(sketch, "E256", {"start": v(76.63, 183.78) * mm, "mid": v(77.89, 181.87) * mm, "end": v(79.46, 180.22) * mm});
            skLineSegment(sketch, "E257", {"start": v(85.53, 181.9) * mm, "end": v(84.76, 177.46) * mm});
            skLineSegment(sketch, "E258", {"start": v(69.91, 187.1) * mm, "end": v(75.8, 185.69) * mm});
            skArc(sketch, "E259", {"start": v(75.13, 190.18) * mm, "mid": v(75.26, 187.9) * mm, "end": v(75.8, 185.69) * mm});
            skLineSegment(sketch, "E260", {"start": v(81.2, 172.93) * mm, "end": v(81.14, 178.98) * mm});
            skArc(sketch, "E261", {"start": v(81.14, 178.98) * mm, "mid": v(82.9, 178.08) * mm, "end": v(84.76, 177.46) * mm});
            skLineSegment(sketch, "E262", {"start": v(88.9, 186.31) * mm, "end": v(81.43, 143.36) * mm});
            skArc(sketch, "E263", {"start": v(88.33, 197.99) * mm, "mid": v(79.74, 191.2) * mm, "end": v(85.53, 181.9) * mm});
            skArc(sketch, "E264", {"start": v(86.99, 199.22) * mm, "mid": v(78.5, 191.41) * mm, "end": v(83.86, 181.2) * mm});
            skLineSegment(sketch, "E265", {"start": v(83.86, 181.2) * mm, "end": v(83.6, 179.69) * mm});
            skFitSpline(sketch, "E266", {"points": [v(63.02, 174.48) * mm, v(63.38, 175.26) * mm, v(64.42, 177.58) * mm, v(65.69, 182.73) * mm, v(66.72, 189.18) * mm, v(66.93, 194.9) * mm, v(66.76, 197.89) * mm, v(66.69, 198.76) * mm]});
            skFitSpline(sketch, "E267", {"points": [v(61.5, 178.07) * mm, v(61.54, 178.18) * mm, v(61.66, 178.53) * mm, v(61.93, 179.38) * mm, v(62.27, 180.65) * mm, v(62.63, 182.23) * mm, v(62.96, 183.85) * mm, v(63.25, 185.47) * mm, v(63.5, 187.1) * mm, v(63.7, 188.73) * mm, v(63.87, 190.36) * mm, v(63.98, 191.98) * mm, v(64.05, 193.61) * mm, v(64.06, 195.23) * mm, v(64, 196.85) * mm, v(63.92, 198.26) * mm, v(63.84, 199.14) * mm, v(63.8, 199.55) * mm]});
            skLineSegment(sketch, "E268", {"start": v(41.4, 180.52) * mm, "end": v(37.46, 198.9) * mm});
            skLineSegment(sketch, "E269", {"start": v(43.77, 182.87) * mm, "end": v(41.4, 180.52) * mm});
            skArc(sketch, "E270", {"start": v(61.6, 173.9) * mm, "mid": v(52.12, 176.95) * mm, "end": v(42.48, 179.44) * mm});
            skLineSegment(sketch, "E271", {"start": v(44.84, 181.77) * mm, "end": v(42.48, 179.44) * mm});
            skArc(sketch, "E272", {"start": v(50.57, 180.3) * mm, "mid": v(47.7, 181.06) * mm, "end": v(44.84, 181.77) * mm});
            skLineSegment(sketch, "E273", {"start": v(43.77, 182.87) * mm, "end": v(40.23, 199.36) * mm});
            skLineSegment(sketch, "E274", {"start": v(21.8, 186.47) * mm, "end": v(23.32, 183.5) * mm});
            skLineSegment(sketch, "E275", {"start": v(20.43, 185.77) * mm, "end": v(21.95, 182.8) * mm});
            skLineSegment(sketch, "E276", {"start": v(3.9, 184.71) * mm, "end": v(9.67, 187.47) * mm});
            skLineSegment(sketch, "E277", {"start": v(5.27, 183.67) * mm, "end": v(10.92, 186.37) * mm});
            skArc(sketch, "E278", {"start": v(20.5, 185.65) * mm, "mid": v(20.41, 185.74) * mm, "end": v(20.3, 185.78) * mm});
            skLineSegment(sketch, "E279", {"start": v(84.6, 176.5) * mm, "end": v(79.66, 148.12) * mm});
            skLineSegment(sketch, "E280", {"start": v(69.91, 187.1) * mm, "end": v(75.13, 190.18) * mm});
            skLineSegment(sketch, "E281", {"start": v(70.97, 196.42) * mm, "end": v(75.36, 192.25) * mm});
            skLineSegment(sketch, "E282", {"start": v(70.97, 196.42) * mm, "end": v(77.02, 196.48) * mm});
            skArc(sketch, "E283", {"start": v(77.02, 196.48) * mm, "mid": v(76, 194.44) * mm, "end": v(75.36, 192.25) * mm});
            skLineSegment(sketch, "E284", {"start": v(76.54, 203.97) * mm, "end": v(78.26, 198.16) * mm});
            skLineSegment(sketch, "E285", {"start": v(76.54, 203.97) * mm, "end": v(81.82, 201) * mm});
            skArc(sketch, "E286", {"start": v(81.82, 201) * mm, "mid": v(79.91, 199.74) * mm, "end": v(78.26, 198.16) * mm});
            skLineSegment(sketch, "E287", {"start": v(85.14, 207.71) * mm, "end": v(83.73, 201.82) * mm});
            skLineSegment(sketch, "E288", {"start": v(85.14, 207.71) * mm, "end": v(88.22, 202.5) * mm});
            skArc(sketch, "E289", {"start": v(88.22, 202.5) * mm, "mid": v(85.95, 202.36) * mm, "end": v(83.73, 201.82) * mm});
            skLineSegment(sketch, "E290", {"start": v(81.2, 172.93) * mm, "end": v(84.6, 176.5) * mm});
            skLineSegment(sketch, "E291", {"start": v(87.25, 200.73) * mm, "end": v(86.99, 199.22) * mm});
            skLineSegment(sketch, "E292", {"start": v(77.5, 221.37) * mm, "end": v(80.68, 225.62) * mm});
            skArc(sketch, "E293", {"start": v(60.12, 177.38) * mm, "mid": v(58.88, 177.8) * mm, "end": v(57.64, 178.2) * mm});
            skLineSegment(sketch, "E294", {"start": v(64.2, 201.02) * mm, "end": v(68.76, 207.13) * mm});
            skLineSegment(sketch, "E295", {"start": v(67.1, 200.23) * mm, "end": v(64.2, 201.02) * mm});
            skLineSegment(sketch, "E296", {"start": v(66.69, 198.76) * mm, "end": v(63.8, 199.55) * mm});
            skLineSegment(sketch, "E297", {"start": v(60.12, 177.38) * mm, "end": v(61.6, 173.9) * mm});
            skLineSegment(sketch, "E298", {"start": v(61.5, 178.07) * mm, "end": v(63.02, 174.48) * mm});
            skLineSegment(sketch, "E299", {"start": v(14.73, 206.61) * mm, "end": v(14.73, 200.27) * mm});
            skLineSegment(sketch, "E300", {"start": v(13.2, 196.4) * mm, "end": v(9.67, 187.47) * mm});
            skLineSegment(sketch, "E301", {"start": v(0.77, 241.88) * mm, "end": v(0.77, 224.32) * mm});
            skLineSegment(sketch, "E302", {"start": v(-0.77, 241.88) * mm, "end": v(-0.77, 224.32) * mm});
            skArc(sketch, "E303", {"start": v(0.83, 242.03) * mm, "mid": v(0.79, 241.96) * mm, "end": v(0.77, 241.88) * mm});
            skArc(sketch, "E304", {"start": v(-0.77, 241.88) * mm, "mid": v(-0.79, 241.96) * mm, "end": v(-0.83, 242.03) * mm});
            skArc(sketch, "E305", {"start": v(0.77, 224.32) * mm, "mid": v(0.78, 224.28) * mm, "end": v(0.8, 224.23) * mm});
            skArc(sketch, "E306", {"start": v(-0.8, 224.23) * mm, "mid": v(-0.78, 224.28) * mm, "end": v(-0.77, 224.32) * mm});
            skCircle(sketch, "E307", {"center": v(22.64, 246.5) * mm, "radius": 3.66 * mm});
            skArc(sketch, "E308", {"start": v(-17.34, 247.3) * mm, "mid": v(-17.64, 247.4) * mm, "end": v(-17.79, 247.11) * mm});
            skArc(sketch, "E309", {"start": v(-22.2, 241.62) * mm, "mid": v(-22.45, 241.42) * mm, "end": v(-22.3, 241.15) * mm});
            skArc(sketch, "E310", {"start": v(23, 241.15) * mm, "mid": v(27.61, 242.5) * mm, "end": v(27.94, 247.3) * mm});
            skArc(sketch, "E311", {"start": v(23.07, 241.62) * mm, "mid": v(26.62, 243.3) * mm, "end": v(27.5, 247.11) * mm});
            skArc(sketch, "E312", {"start": v(27.94, 247.3) * mm, "mid": v(27.64, 247.4) * mm, "end": v(27.5, 247.11) * mm});
            skArc(sketch, "E313", {"start": v(23.07, 241.62) * mm, "mid": v(22.83, 241.42) * mm, "end": v(23, 241.15) * mm});
            skCircle(sketch, "E314", {"center": v(-0.7, 255.28) * mm, "radius": 4.36 * mm});
            skArc(sketch, "E315", {"start": v(-1.37, 249.63) * mm, "mid": v(4.27, 249.84) * mm, "end": v(4.99, 255.44) * mm});
            skArc(sketch, "E316", {"start": v(-1.14, 250.06) * mm, "mid": v(3.26, 250.95) * mm, "end": v(4.54, 255.24) * mm});
            skArc(sketch, "E317", {"start": v(-1.14, 250.06) * mm, "mid": v(-1.43, 249.94) * mm, "end": v(-1.37, 249.63) * mm});
            skArc(sketch, "E318", {"start": v(4.99, 255.44) * mm, "mid": v(4.68, 255.53) * mm, "end": v(4.54, 255.24) * mm});
            skArc(sketch, "E319", {"start": v(18.6, 134.7) * mm, "mid": v(39.76, 137.67) * mm, "end": v(60.48, 142.9) * mm});
            skArc(sketch, "E320", {"start": v(15.98, 139.92) * mm, "mid": v(38.29, 140.51) * mm, "end": v(60.48, 142.9) * mm});
            skArc(sketch, "E321", {"start": v(15.98, 139.92) * mm, "mid": v(34.97, 142.56) * mm, "end": v(53.47, 147.58) * mm});
            skArc(sketch, "E322", {"start": v(11.9, 144.33) * mm, "mid": v(32.75, 145.16) * mm, "end": v(53.47, 147.58) * mm});
            skArc(sketch, "E323", {"start": v(11.9, 144.33) * mm, "mid": v(30.94, 147.44) * mm, "end": v(49.67, 152.1) * mm});
            skEllipticalArc(sketch, "E324", {});
            skFitSpline(sketch, "E325", {"points": [v(81.5, 144.14) * mm, v(81.5, 144.94) * mm, v(81.1, 146.45) * mm, v(80.15, 147.63) * mm, v(79.66, 148.12) * mm]});
            skFitSpline(sketch, "E326", {"points": [v(-79.66, 148.12) * mm, v(-80.15, 147.63) * mm, v(-81.1, 146.44) * mm, v(-81.55, 144.75) * mm, v(-81.49, 143.75) * mm, v(-81.43, 143.36) * mm]});
            skFitSpline(sketch, "E327", {"points": [v(81.43, 143.36) * mm, v(81.49, 143.74) * mm, v(81.5, 143.94) * mm, v(81.5, 144.14) * mm]});
            skEllipticalArc(sketch, "E328", {});
            skArc(sketch, "E329", {"start": v(-11.9, 144.33) * mm, "mid": v(-30.94, 147.44) * mm, "end": v(-49.67, 152.1) * mm});
            skArc(sketch, "E330", {"start": v(-11.9, 144.33) * mm, "mid": v(-32.75, 145.16) * mm, "end": v(-53.47, 147.58) * mm});
            skArc(sketch, "E331", {"start": v(-15.98, 139.92) * mm, "mid": v(-34.97, 142.56) * mm, "end": v(-53.47, 147.58) * mm});
            skArc(sketch, "E332", {"start": v(-15.98, 139.92) * mm, "mid": v(-38.29, 140.51) * mm, "end": v(-60.48, 142.9) * mm});
            skArc(sketch, "E333", {"start": v(-18.6, 134.7) * mm, "mid": v(-39.76, 137.67) * mm, "end": v(-60.48, 142.9) * mm});
            skEllipticalArc(sketch, "E334", {});
            skEllipticalArc(sketch, "E335", {});
            skLineSegment(sketch, "E336", {"start": v(35.44, 262.8) * mm, "end": v(39.8, 267.43) * mm});
            skLineSegment(sketch, "E337", {"start": v(36.5, 261.6) * mm, "end": v(40.86, 266.24) * mm});
            skLineSegment(sketch, "E338", {"start": v(-14.73, 253.63) * mm, "end": v(-35.44, 262.8) * mm});
            skLineSegment(sketch, "E339", {"start": v(-14.73, 256.34) * mm, "end": v(-39.8, 267.43) * mm});
            skLineSegment(sketch, "E340", {"start": v(-36.5, 261.6) * mm, "end": v(-14.73, 206.61) * mm});
            skLineSegment(sketch, "E341", {"start": v(-40.86, 266.24) * mm, "end": v(-14.73, 200.27) * mm});
            skLineSegment(sketch, "E342", {"start": v(-35.44, 262.8) * mm, "end": v(-39.8, 267.43) * mm});
            skLineSegment(sketch, "E343", {"start": v(-36.5, 261.6) * mm, "end": v(-40.86, 266.24) * mm});
            skLineSegment(sketch, "E344", {"start": v(-236.57, 637.72) * mm, "end": v(-198.67, 637.72) * mm});
            skFitSpline(sketch, "E345", {"points": [v(-237.94, 455.24) * mm, v(-237.78, 455.7) * mm, v(-236.87, 458.23) * mm, v(-235.39, 462.89) * mm, v(-233.6, 469.25) * mm, v(-232.1, 475.67) * mm, v(-230.47, 484.16) * mm, v(-229.23, 492.68) * mm, v(-227.96, 501.2) * mm, v(-227.2, 509.76) * mm, v(-226.43, 520.42) * mm, v(-225.83, 533.18) * mm, v(-225.68, 545.94) * mm, v(-225.85, 558.68) * mm, v(-226.09, 569.34) * mm, v(-226.57, 577.93) * mm, v(-227.41, 586.48) * mm, v(-228.64, 597.15) * mm, v(-230.38, 607.75) * mm, v(-232, 616.19) * mm, v(-233.6, 622.45) * mm, v(-235.1, 628.8) * mm, v(-236.77, 633.54) * mm, v(-237.7, 636.2) * mm, v(-237.9, 636.76) * mm]});
            skFitSpline(sketch, "E346", {"points": [v(-197.05, 636.93) * mm, v(-197.2, 636.5) * mm, v(-198.08, 634.02) * mm, v(-199.41, 629.5) * mm, v(-200.84, 624.38) * mm, v(-201.96, 620.24) * mm, v(-202.88, 616.06) * mm, v(-203.95, 610.85) * mm, v(-205, 604.64) * mm, v(-205.97, 598.4) * mm, v(-206.74, 592.15) * mm, v(-207.4, 585.9) * mm, v(-207.95, 579.67) * mm, v(-208.54, 571.39) * mm, v(-208.97, 563.1) * mm, v(-209.31, 554.8) * mm, v(-209.4, 550.6) * mm, v(-209.41, 548.46) * mm]});
            skLineSegment(sketch, "E347", {"start": v(-209.41, 548.46) * mm, "end": v(-209.41, 475.84) * mm});
            skLineSegment(sketch, "E348", {"start": v(-208.3, 474.78) * mm, "end": v(-88.27, 474.78) * mm});
            skFitSpline(sketch, "E349", {"points": [v(-88.27, 474.78) * mm, v(-86.65, 474.9) * mm, v(-83.35, 475.15) * mm, v(-76.82, 475.8) * mm, v(-71.03, 476.66) * mm, v(-66, 477.41) * mm, v(-62.78, 478.14) * mm, v(-58.8, 479.05) * mm, v(-54.74, 479.7) * mm, v(-51.33, 480.57) * mm, v(-48.73, 481.33) * mm, v(-46.18, 482.19) * mm, v(-42.96, 483.38) * mm, v(-39.2, 485.04) * mm, v(-35.3, 486.5) * mm, v(-32.13, 487.86) * mm, v(-29, 489.46) * mm, v(-26.56, 490.84) * mm, v(-24.9, 491.75) * mm, v(-24.68, 491.88) * mm]});
            skFitSpline(sketch, "E350", {"points": [v(-25.73, 486.38) * mm, v(-25.82, 485.88) * mm, v(-26.15, 484.2) * mm, v(-26.8, 481.37) * mm, v(-27.75, 477.87) * mm, v(-28.82, 474.4) * mm, v(-30.02, 470.94) * mm, v(-31.31, 467.54) * mm, v(-32.75, 464.2) * mm, v(-34.31, 460.88) * mm, v(-35.82, 457.87) * mm, v(-36.84, 456) * mm, v(-37.28, 455.2) * mm]});
            skLineSegment(sketch, "E351", {"start": v(-38.57, 454.36) * mm, "end": v(-236.47, 454.36) * mm});
            skLineSegment(sketch, "E352", {"start": v(17.74, 637.72) * mm, "end": v(236.57, 637.72) * mm});
            skLineSegment(sketch, "E353", {"start": v(46.17, 617.52) * mm, "end": v(208.14, 617.52) * mm});
            skLineSegment(sketch, "E354", {"start": v(46.17, 548.98) * mm, "end": v(208.14, 548.98) * mm});
            skLineSegment(sketch, "E355", {"start": v(46.17, 528.52) * mm, "end": v(208.14, 528.52) * mm});
            skLineSegment(sketch, "E356", {"start": v(45.08, 455.44) * mm, "end": v(45.08, 527.44) * mm});
            skLineSegment(sketch, "E357", {"start": v(44, 454.36) * mm, "end": v(17.84, 454.36) * mm});
            skFitSpline(sketch, "E358", {"points": [v(16.36, 455.24) * mm, v(16.53, 455.7) * mm, v(17.44, 458.23) * mm, v(18.92, 462.89) * mm, v(20.7, 469.25) * mm, v(22.2, 475.67) * mm, v(23.84, 484.16) * mm, v(25.07, 492.68) * mm, v(26.35, 501.2) * mm, v(27.1, 509.76) * mm, v(27.88, 520.42) * mm, v(28.48, 533.18) * mm, v(28.62, 545.94) * mm, v(28.45, 558.68) * mm, v(28.21, 569.34) * mm, v(27.74, 577.93) * mm, v(26.9, 586.48) * mm, v(25.67, 597.15) * mm, v(23.92, 607.75) * mm, v(22.3, 616.19) * mm, v(20.7, 622.45) * mm, v(19.2, 628.8) * mm, v(17.54, 633.54) * mm, v(16.6, 636.2) * mm, v(16.41, 636.76) * mm]});
            skLineSegment(sketch, "E359", {"start": v(45.08, 550.06) * mm, "end": v(45.08, 616.44) * mm});
            skLineSegment(sketch, "E360", {"start": v(209.22, 550.06) * mm, "end": v(209.22, 616.44) * mm});
            skFitSpline(sketch, "E361", {"points": [v(237.94, 455.24) * mm, v(237.78, 455.7) * mm, v(236.87, 458.23) * mm, v(235.39, 462.89) * mm, v(233.6, 469.25) * mm, v(232.1, 475.67) * mm, v(230.47, 484.16) * mm, v(229.23, 492.68) * mm, v(227.96, 501.2) * mm, v(227.2, 509.76) * mm, v(226.43, 520.42) * mm, v(225.83, 533.18) * mm, v(225.68, 545.94) * mm, v(225.85, 558.68) * mm, v(226.09, 569.34) * mm, v(226.57, 577.93) * mm, v(227.41, 586.48) * mm, v(228.64, 597.15) * mm, v(230.38, 607.75) * mm, v(232, 616.19) * mm, v(233.6, 622.45) * mm, v(235.1, 628.8) * mm, v(236.77, 633.54) * mm, v(237.7, 636.2) * mm, v(237.9, 636.76) * mm]});
            skLineSegment(sketch, "E362", {"start": v(209.22, 455.44) * mm, "end": v(209.22, 527.44) * mm});
            skLineSegment(sketch, "E363", {"start": v(236.47, 454.36) * mm, "end": v(210.3, 454.36) * mm});
            skLineSegment(sketch, "E364", {"start": v(-1.59, 24.9) * mm, "end": v(-1.59, 48.66) * mm});
            skLineSegment(sketch, "E365", {"start": v(1.59, 24.9) * mm, "end": v(1.59, 48.66) * mm});
            skLineSegment(sketch, "E366", {"start": v(-285.55, 232) * mm, "end": v(-266.3, 241.83) * mm});
            skLineSegment(sketch, "E367", {"start": v(-284.1, 229.17) * mm, "end": v(-264.85, 239) * mm});
            skLineSegment(sketch, "E368", {"start": v(-285.55, 353.32) * mm, "end": v(-266.3, 321.91) * mm});
            skLineSegment(sketch, "E369", {"start": v(-283.69, 356.35) * mm, "end": v(-264.43, 324.95) * mm});
            skLineSegment(sketch, "E370", {"start": v(-266.3, 402.83) * mm, "end": v(-285.55, 376.71) * mm});
            skLineSegment(sketch, "E371", {"start": v(-264.32, 400.16) * mm, "end": v(-283.58, 374.04) * mm});
            skLineSegment(sketch, "E372", {"start": v(-285.55, 708.6) * mm, "end": v(-266.3, 689.34) * mm});
            skLineSegment(sketch, "E373", {"start": v(-283.3, 710.84) * mm, "end": v(-264.05, 691.59) * mm});
            skLineSegment(sketch, "E374", {"start": v(283.3, 710.84) * mm, "end": v(264.05, 691.59) * mm});
            skLineSegment(sketch, "E375", {"start": v(285.55, 708.6) * mm, "end": v(266.3, 689.34) * mm});
            skLineSegment(sketch, "E376", {"start": v(264.32, 400.16) * mm, "end": v(283.58, 374.04) * mm});
            skLineSegment(sketch, "E377", {"start": v(266.3, 402.83) * mm, "end": v(285.55, 376.71) * mm});
            skLineSegment(sketch, "E378", {"start": v(283.69, 356.35) * mm, "end": v(264.43, 324.95) * mm});
            skLineSegment(sketch, "E379", {"start": v(285.55, 353.32) * mm, "end": v(266.3, 321.91) * mm});
            skLineSegment(sketch, "E380", {"start": v(285.55, 232) * mm, "end": v(266.3, 241.83) * mm});
            skLineSegment(sketch, "E381", {"start": v(284.1, 229.17) * mm, "end": v(264.85, 239) * mm});
            skLineSegment(sketch, "E382", {"start": v(0, 0) * mm, "end": v(304.8, 220.37) * mm});
            const initialGuessF0  = {"E324": [0, 0.1441398184, 1, 0, 0.0791222954, 0.0135710168, 0, 3.141592653589793], "E328": [0, 0.1441398184, 1, 0, 0.0679798488, 0.011659870000000001, 0.751609, 2.389983], "E334": [0, 0.1441398184, 1, 0, 0.0791222954, 0.0097111058, 3.141592653589793, 4.475042], "E335": [0, 0.1441398184, 1, 0, 0.0791222954, 0.0097111058, 4.949736, 0]};
            skSetInitialGuess(sketch, initialGuessF0);
            skSolve(sketch);
        }
        {
            var Q0;
            Q0 = qSketchRegion(id + "F0", true);
            extrude(context, id + "F1", {"entities" : qUnion([Q0]), "depth" : 3.17 * mm});
        }
    });
